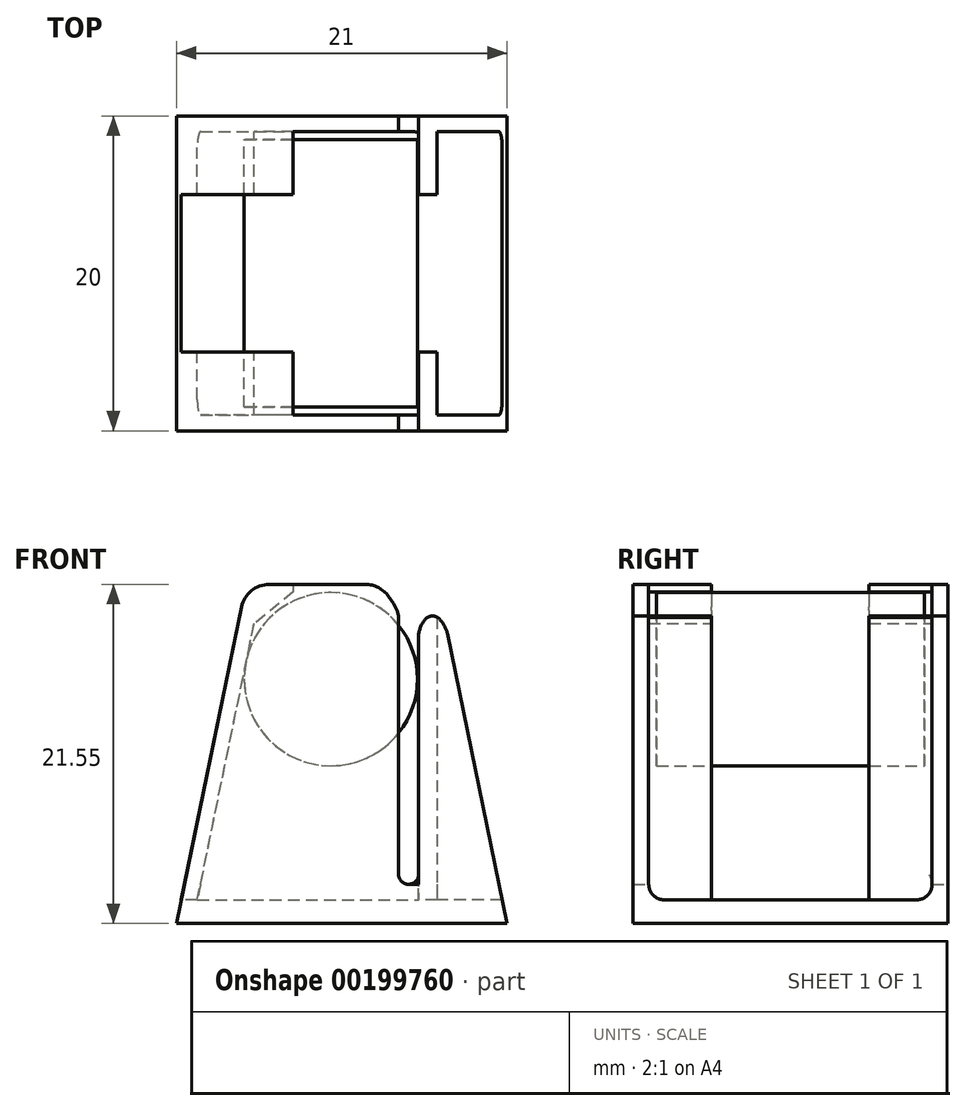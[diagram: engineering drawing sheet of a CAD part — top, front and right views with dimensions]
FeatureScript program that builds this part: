
annotation { "Feature Type Name" : "Feature", "Feature Type Description" : "" }
export const myFeature = defineFeature(function(context is Context, id is Id, definition is map)
    precondition{}
    {
        {
            var Q0;
            Q0=qCreatedBy(makeId("Front.planeOp"),FACE);
            var sketch = newSketch(context, id + "F0", { "sketchPlane" : qUnion([Q0])});
            skLineSegment(sketch, "E0", {"start": v(-14.75, 0) * mm, "end": v(-10.32, 21.55) * mm});
            skLineSegment(sketch, "E1", {"start": v(-1.82, 21.55) * mm, "end": v(0, 18.96) * mm});
            skLineSegment(sketch, "E2", {"start": v(0, 18.96) * mm, "end": v(1.82, 21.55) * mm});
            skLineSegment(sketch, "E3", {"start": v(1.82, 21.55) * mm, "end": v(6.25, 0) * mm});
            skCircle(sketch, "E4", {"center": v(-6.3, 7.31) * mm, "radius": 5.5 * mm});
            skLineSegment(sketch, "E5", {"start": v(-14.75, 0) * mm, "end": v(6.25, 0) * mm});
            skLineSegment(sketch, "E6", {"start": v(5.94, 1.5) * mm, "end": v(-14.44, 1.5) * mm});
            skLineSegment(sketch, "E7.left", {"start": v(-0.63, 19.86) * mm, "end": v(-0.63, 1.5) * mm});
            skLineSegment(sketch, "E8.0", {"start": v(-13.73, 0) * mm, "end": v(-9.3, 21.55) * mm});
            skLineSegment(sketch, "E9.0", {"start": v(1.82, 21.55) * mm, "end": v(1.82, 1.5) * mm});
            skLineSegment(sketch, "E10", {"start": v(-10.32, 21.55) * mm, "end": v(-1.82, 21.55) * mm});
            skLineSegment(sketch, "E11", {"start": v(-0.63, 2.5) * mm, "end": v(0.63, 2.5) * mm});
            skLineSegment(sketch, "E12", {"start": v(0.63, 1.5) * mm, "end": v(0.63, 19.86) * mm});
            skLineSegment(sketch, "E13.bottom", {"start": v(13.14, 28.72) * mm, "end": v(0.63, 28.72) * mm});
            skLineSegment(sketch, "E13.top", {"start": v(13.14, 19.86) * mm, "end": v(0.63, 19.86) * mm});
            skLineSegment(sketch, "E13.left", {"start": v(13.14, 28.72) * mm, "end": v(13.14, 19.86) * mm});
            skLineSegment(sketch, "E13.right", {"start": v(0.63, 28.72) * mm, "end": v(0.63, 19.86) * mm});
            skSolve(sketch);
        }
        {
            var Q0;
            {var subQ5=sQuery(id+"F0.wireOp",EDGE,"E0");var subQ8=sQuery(id+"F0.wireOp",EDGE,"E10");var subQ10=makeQuery(id+"F0.imprint","INTERSECT",VERTEX,{"derivedFrom":[subQ5,subQ8]});Q0=makeQuery(id+"F0.imprint","IMPRINT",FACE,{"disambiguationData":[TD([[makeQuery(id+"F0.imprint","IMPRINT",EDGE,{"disambiguationData":[TD([[subQ10,1.0]])],"derivedFrom":subQ5}),-1.0]])]});}
            var Q1;
            {var subQ0=sQuery(id+"F0.wireOp",EDGE,"E5");var subQ1=sQuery(id+"F0.wireOp",EDGE,"E0");var subQ2=makeQuery(id+"F0.imprint","INTERSECT",VERTEX,{"derivedFrom":[subQ1,subQ0]});Q1=makeQuery(id+"F0.imprint","IMPRINT",FACE,{"disambiguationData":[TD([[makeQuery(id+"F0.imprint","IMPRINT",EDGE,{"disambiguationData":[TD([[subQ2,-1.0]])],"derivedFrom":subQ1}),-1.0]])]});}
            var Q2;
            {var subQ0=sQuery(id+"F0.wireOp",EDGE,"E7.left");var subQ5=sQuery(id+"F0.wireOp",EDGE,"E6");var subQ6=makeQuery(id+"F0.imprint","INTERSECT",VERTEX,{"derivedFrom":[subQ5,subQ0]});Q2=makeQuery(id+"F0.imprint","IMPRINT",FACE,{"disambiguationData":[TD([[makeQuery(id+"F0.imprint","IMPRINT",EDGE,{"disambiguationData":[TD([[subQ6,-1.0]])],"derivedFrom":subQ5}),1.0]])]});}
            var Q3;
            {var subQ5=sQuery(id+"F0.wireOp",EDGE,"E7.top");Q3=makeQuery(id+"F0.imprint","IMPRINT",FACE,{"disambiguationData":[TD([[makeQuery(id+"F0.imprint","IMPRINT",EDGE,{"derivedFrom":subQ5}),1.0]])]});}
            var Q4;
            {var subQ3=sQuery(id+"F0.wireOp",EDGE,"E9.0");var subQ5=sQuery(id+"F0.wireOp",EDGE,"E6");var subQ7=makeQuery(id+"F0.imprint","INTERSECT",VERTEX,{"derivedFrom":[subQ5,subQ3]});Q4=makeQuery(id+"F0.imprint","IMPRINT",FACE,{"disambiguationData":[TD([[makeQuery(id+"F0.imprint","IMPRINT",EDGE,{"disambiguationData":[TD([[subQ7,-1.0]])],"derivedFrom":subQ5}),1.0]])]});}
            var Q5;
            {var subQ3=sQuery(id+"F0.wireOp",EDGE,"E6");var subQ5=sQuery(id+"F0.wireOp",EDGE,"E9.0");var subQ6=makeQuery(id+"F0.imprint","INTERSECT",VERTEX,{"derivedFrom":[subQ3,subQ5]});Q5=makeQuery(id+"F0.imprint","IMPRINT",FACE,{"disambiguationData":[TD([[makeQuery(id+"F0.imprint","IMPRINT",EDGE,{"disambiguationData":[TD([[subQ6,-1.0]])],"derivedFrom":subQ3}),-1.0]])]});}
            var Q6;
            {var subQ1=sQuery(id+"F0.wireOp",EDGE,"E3");var subQ3=sQuery(id+"F0.wireOp",EDGE,"E6");var subQ4=makeQuery(id+"F0.imprint","INTERSECT",VERTEX,{"derivedFrom":[subQ1,subQ3]});Q6=makeQuery(id+"F0.imprint","IMPRINT",FACE,{"disambiguationData":[TD([[makeQuery(id+"F0.imprint","IMPRINT",EDGE,{"disambiguationData":[TD([[subQ4,-1.0]])],"derivedFrom":subQ3}),-1.0]])]});}
            var Q7;
            {var subQ0=sQuery(id+"F0.wireOp",EDGE,"E5");var subQ1=sQuery(id+"F0.wireOp",EDGE,"E3");var subQ2=makeQuery(id+"F0.imprint","INTERSECT",VERTEX,{"derivedFrom":[subQ1,subQ0]});Q7=makeQuery(id+"F0.imprint","IMPRINT",FACE,{"disambiguationData":[TD([[makeQuery(id+"F0.imprint","IMPRINT",EDGE,{"disambiguationData":[TD([[subQ2,1.0]])],"derivedFrom":subQ1}),-1.0]])]});}
            var Q8;
            {var subQ5=sQuery(id+"F0.wireOp",EDGE,"E11");Q8=makeQuery(id+"F0.imprint","IMPRINT",FACE,{"disambiguationData":[TD([[makeQuery(id+"F0.imprint","IMPRINT",EDGE,{"derivedFrom":subQ5}),-1.0]])]});}
            var Q9;
            {var subQ4=sQuery(id+"F0.wireOp",EDGE,"E10");var subQ7=sQuery(id+"F0.wireOp",EDGE,"E1");var subQ8=makeQuery(id+"F0.imprint","INTERSECT",VERTEX,{"derivedFrom":[subQ7,subQ4]});Q9=makeQuery(id+"F0.imprint","IMPRINT",FACE,{"disambiguationData":[TD([[makeQuery(id+"F0.imprint","IMPRINT",EDGE,{"disambiguationData":[TD([[subQ8,-1.0]])],"derivedFrom":subQ7}),-1.0]])]});}
            var Q10;
            Q10=makeQuery(id+"F0.imprint","IMPRINT",FACE,{"disambiguationData":[TD([[makeQuery(id+"F0.imprint","IMPRINT",EDGE,{"derivedFrom":sQuery(id+"F0.wireOp",EDGE,"E4")}),1.0]])]});
            extrude(context, id + "F1", {"entities" : qUnion([Q0, Q1, Q2, Q3, Q4, Q5, Q6, Q7, Q8, Q9, Q10]), "depth" : 1 * mm});
        }
        {
            var Q0;
            {var subQ2=sQuery(id+"F0.wireOp",EDGE,"E6");var subQ4=sQuery(id+"F0.wireOp",EDGE,"E9.0");var subQ5=makeQuery(id+"F0.imprint","INTERSECT",VERTEX,{"derivedFrom":[subQ2,subQ4]});Q0=makeQuery(id+"F0.imprint","IMPRINT",FACE,{"disambiguationData":[TD([[makeQuery(id+"F0.imprint","IMPRINT",EDGE,{"disambiguationData":[TD([[subQ5,-1.0]])],"derivedFrom":subQ2}),-1.0]])]});}
            var Q1;
            {var subQ0=sQuery(id+"F0.wireOp",EDGE,"E10");var subQ1=sQuery(id+"F0.wireOp",EDGE,"E0");var subQ2=makeQuery(id+"F0.imprint","INTERSECT",VERTEX,{"derivedFrom":[subQ1,subQ0]});Q1=makeQuery(id+"F0.imprint","IMPRINT",FACE,{"disambiguationData":[TD([[makeQuery(id+"F0.imprint","IMPRINT",EDGE,{"disambiguationData":[TD([[subQ2,1.0]])],"derivedFrom":subQ1}),-1.0]])]});}
            extrude(context, id + "F2", {"entities" : qUnion([Q0, Q1]), "operationType" : NewBodyOperationType.ADD, "depth" : 5 * mm, "hasSecondDirection" : true, "secondDirectionOppositeDirection" : false, "secondDirectionDepth" : 1 * mm});
        }
        {
            var Q0;
            {var subQ0=sQuery(id+"F0.wireOp",EDGE,"E5");var subQ1=sQuery(id+"F0.wireOp",EDGE,"E3");var subQ2=makeQuery(id+"F0.imprint","INTERSECT",VERTEX,{"derivedFrom":[subQ1,subQ0]});Q0=makeQuery(id+"F0.imprint","IMPRINT",FACE,{"disambiguationData":[TD([[makeQuery(id+"F0.imprint","IMPRINT",EDGE,{"disambiguationData":[TD([[subQ2,1.0]])],"derivedFrom":subQ1}),-1.0]])]});}
            var Q1;
            {var subQ5=sQuery(id+"F0.wireOp",EDGE,"E7.top");Q1=makeQuery(id+"F0.imprint","IMPRINT",FACE,{"disambiguationData":[TD([[makeQuery(id+"F0.imprint","IMPRINT",EDGE,{"derivedFrom":subQ5}),1.0]])]});}
            var Q2;
            {var subQ3=sQuery(id+"F0.wireOp",EDGE,"E9.0");var subQ5=sQuery(id+"F0.wireOp",EDGE,"E6");var subQ6=makeQuery(id+"F0.imprint","INTERSECT",VERTEX,{"derivedFrom":[subQ5,subQ3]});Q2=makeQuery(id+"F0.imprint","IMPRINT",FACE,{"disambiguationData":[TD([[makeQuery(id+"F0.imprint","IMPRINT",EDGE,{"disambiguationData":[TD([[subQ6,-1.0]])],"derivedFrom":subQ5}),1.0]])]});}
            var Q3;
            {var subQ0=sQuery(id+"F0.wireOp",EDGE,"E7.left");var subQ5=sQuery(id+"F0.wireOp",EDGE,"E6");var subQ6=makeQuery(id+"F0.imprint","INTERSECT",VERTEX,{"derivedFrom":[subQ5,subQ0]});Q3=makeQuery(id+"F0.imprint","IMPRINT",FACE,{"disambiguationData":[TD([[makeQuery(id+"F0.imprint","IMPRINT",EDGE,{"disambiguationData":[TD([[subQ6,-1.0]])],"derivedFrom":subQ5}),1.0]])]});}
            var Q4;
            {var subQ0=sQuery(id+"F0.wireOp",EDGE,"E5");var subQ1=sQuery(id+"F0.wireOp",EDGE,"E0");var subQ2=makeQuery(id+"F0.imprint","INTERSECT",VERTEX,{"derivedFrom":[subQ1,subQ0]});Q4=makeQuery(id+"F0.imprint","IMPRINT",FACE,{"disambiguationData":[TD([[makeQuery(id+"F0.imprint","IMPRINT",EDGE,{"disambiguationData":[TD([[subQ2,-1.0]])],"derivedFrom":subQ1}),-1.0]])]});}
            extrude(context, id + "F3", {"entities" : qUnion([Q0, Q1, Q2, Q3, Q4]), "operationType" : NewBodyOperationType.ADD, "depth" : 20 * mm});
        }
        {
            var Q0;
            {var subQ2=sQuery(id+"F0.wireOp",EDGE,"E6");var subQ4=sQuery(id+"F0.wireOp",EDGE,"E9.0");var subQ5=makeQuery(id+"F0.imprint","INTERSECT",VERTEX,{"derivedFrom":[subQ2,subQ4]});Q0=makeQuery(id+"F0.imprint","IMPRINT",FACE,{"disambiguationData":[TD([[makeQuery(id+"F0.imprint","IMPRINT",EDGE,{"disambiguationData":[TD([[subQ5,-1.0]])],"derivedFrom":subQ2}),-1.0]])]});}
            var Q1;
            {var subQ0=sQuery(id+"F0.wireOp",EDGE,"E10");var subQ1=sQuery(id+"F0.wireOp",EDGE,"E0");var subQ2=makeQuery(id+"F0.imprint","INTERSECT",VERTEX,{"derivedFrom":[subQ1,subQ0]});Q1=makeQuery(id+"F0.imprint","IMPRINT",FACE,{"disambiguationData":[TD([[makeQuery(id+"F0.imprint","IMPRINT",EDGE,{"disambiguationData":[TD([[subQ2,1.0]])],"derivedFrom":subQ1}),-1.0]])]});}
            extrude(context, id + "F4", {"entities" : qUnion([Q0, Q1]), "operationType" : NewBodyOperationType.ADD, "depth" : 20 * mm, "hasSecondDirection" : true, "secondDirectionOppositeDirection" : false, "secondDirectionDepth" : 15 * mm});
        }
        {
            var Q0;
            {var subQ1=sQuery(id+"F0.wireOp",EDGE,"E3");var subQ3=sQuery(id+"F0.wireOp",EDGE,"E6");var subQ4=makeQuery(id+"F0.imprint","INTERSECT",VERTEX,{"derivedFrom":[subQ1,subQ3]});Q0=makeQuery(id+"F0.imprint","IMPRINT",FACE,{"disambiguationData":[TD([[makeQuery(id+"F0.imprint","IMPRINT",EDGE,{"disambiguationData":[TD([[subQ4,-1.0]])],"derivedFrom":subQ3}),-1.0]])]});}
            var Q1;
            {var subQ2=sQuery(id+"F0.wireOp",EDGE,"E6");var subQ4=sQuery(id+"F0.wireOp",EDGE,"E9.0");var subQ5=makeQuery(id+"F0.imprint","INTERSECT",VERTEX,{"derivedFrom":[subQ2,subQ4]});Q1=makeQuery(id+"F0.imprint","IMPRINT",FACE,{"disambiguationData":[TD([[makeQuery(id+"F0.imprint","IMPRINT",EDGE,{"disambiguationData":[TD([[subQ5,-1.0]])],"derivedFrom":subQ2}),-1.0]])]});}
            var Q2;
            {var subQ0=sQuery(id+"F0.wireOp",EDGE,"E5");var subQ1=sQuery(id+"F0.wireOp",EDGE,"E3");var subQ2=makeQuery(id+"F0.imprint","INTERSECT",VERTEX,{"derivedFrom":[subQ1,subQ0]});Q2=makeQuery(id+"F0.imprint","IMPRINT",FACE,{"disambiguationData":[TD([[makeQuery(id+"F0.imprint","IMPRINT",EDGE,{"disambiguationData":[TD([[subQ2,1.0]])],"derivedFrom":subQ1}),-1.0]])]});}
            var Q3;
            {var subQ3=sQuery(id+"F0.wireOp",EDGE,"E9.0");var subQ5=sQuery(id+"F0.wireOp",EDGE,"E6");var subQ6=makeQuery(id+"F0.imprint","INTERSECT",VERTEX,{"derivedFrom":[subQ5,subQ3]});Q3=makeQuery(id+"F0.imprint","IMPRINT",FACE,{"disambiguationData":[TD([[makeQuery(id+"F0.imprint","IMPRINT",EDGE,{"disambiguationData":[TD([[subQ6,-1.0]])],"derivedFrom":subQ5}),1.0]])]});}
            var Q4;
            {var subQ5=sQuery(id+"F0.wireOp",EDGE,"E11");Q4=makeQuery(id+"F0.imprint","IMPRINT",FACE,{"disambiguationData":[TD([[makeQuery(id+"F0.imprint","IMPRINT",EDGE,{"derivedFrom":subQ5}),-1.0]])]});}
            var Q5;
            {var subQ5=sQuery(id+"F0.wireOp",EDGE,"E7.top");Q5=makeQuery(id+"F0.imprint","IMPRINT",FACE,{"disambiguationData":[TD([[makeQuery(id+"F0.imprint","IMPRINT",EDGE,{"derivedFrom":subQ5}),1.0]])]});}
            var Q6;
            {var subQ0=sQuery(id+"F0.wireOp",EDGE,"E7.left");var subQ5=sQuery(id+"F0.wireOp",EDGE,"E6");var subQ6=makeQuery(id+"F0.imprint","INTERSECT",VERTEX,{"derivedFrom":[subQ5,subQ0]});Q6=makeQuery(id+"F0.imprint","IMPRINT",FACE,{"disambiguationData":[TD([[makeQuery(id+"F0.imprint","IMPRINT",EDGE,{"disambiguationData":[TD([[subQ6,-1.0]])],"derivedFrom":subQ5}),1.0]])]});}
            var Q7;
            Q7=makeQuery(id+"F0.imprint","IMPRINT",FACE,{"disambiguationData":[TD([[makeQuery(id+"F0.imprint","IMPRINT",EDGE,{"derivedFrom":sQuery(id+"F0.wireOp",EDGE,"diKSwn5I-yN5J-uPFe-3HvR-bQsWpq5G5K9p")}),-1.0]])]});
            var Q8;
            Q8=makeQuery(id+"F0.imprint","IMPRINT",FACE,{"disambiguationData":[TD([[makeQuery(id+"F0.imprint","IMPRINT",EDGE,{"derivedFrom":sQuery(id+"F0.wireOp",EDGE,"E4")}),1.0]])]});
            var Q9;
            Q9=makeQuery(id+"F0.imprint","IMPRINT",FACE,{"disambiguationData":[TD([[makeQuery(id+"F0.imprint","IMPRINT",EDGE,{"derivedFrom":sQuery(id+"F0.wireOp",EDGE,"E4")}),-1.0]])]});
            var Q10;
            {var subQ0=sQuery(id+"F0.wireOp",EDGE,"E10");var subQ1=sQuery(id+"F0.wireOp",EDGE,"E0");var subQ2=makeQuery(id+"F0.imprint","INTERSECT",VERTEX,{"derivedFrom":[subQ1,subQ0]});Q10=makeQuery(id+"F0.imprint","IMPRINT",FACE,{"disambiguationData":[TD([[makeQuery(id+"F0.imprint","IMPRINT",EDGE,{"disambiguationData":[TD([[subQ2,1.0]])],"derivedFrom":subQ1}),-1.0]])]});}
            var Q11;
            {var subQ0=sQuery(id+"F0.wireOp",EDGE,"E5");var subQ1=sQuery(id+"F0.wireOp",EDGE,"E0");var subQ2=makeQuery(id+"F0.imprint","INTERSECT",VERTEX,{"derivedFrom":[subQ1,subQ0]});Q11=makeQuery(id+"F0.imprint","IMPRINT",FACE,{"disambiguationData":[TD([[makeQuery(id+"F0.imprint","IMPRINT",EDGE,{"disambiguationData":[TD([[subQ2,-1.0]])],"derivedFrom":subQ1}),-1.0]])]});}
            extrude(context, id + "F5", {"entities" : qUnion([Q0, Q1, Q2, Q3, Q4, Q5, Q6, Q7, Q8, Q9, Q10, Q11]), "operationType" : NewBodyOperationType.ADD, "depth" : 20 * mm, "hasSecondDirection" : true, "secondDirectionOppositeDirection" : false, "secondDirectionDepth" : 19 * mm});
        }
        {
            var Q0;
            {var subQ0=sQuery(id+"F0.wireOp",EDGE,"E7.left");var subQ1=sQuery(id+"F0.wireOp",EDGE,"E4");var subQ2=makeQuery(id+"F0.imprint","INTERSECT",VERTEX,{"disambiguationData":[OD(0.0)],"derivedFrom":[subQ1,subQ0]});Q0=makeQuery(id+"F0.imprint","IMPRINT",FACE,{"disambiguationData":[TD([[makeQuery(id+"F0.imprint","IMPRINT",EDGE,{"disambiguationData":[TD([[subQ2,-1.0]])],"derivedFrom":subQ1}),1.0]])]});}
            var Q1;
            {var subQ0=sQuery(id+"F0.wireOp",EDGE,"E7.left");var subQ1=sQuery(id+"F0.wireOp",EDGE,"E4");var subQ2=makeQuery(id+"F0.imprint","INTERSECT",VERTEX,{"disambiguationData":[OD(0.0)],"derivedFrom":[subQ1,subQ0]});Q1=makeQuery(id+"F0.imprint","IMPRINT",FACE,{"disambiguationData":[TD([[makeQuery(id+"F0.imprint","IMPRINT",EDGE,{"disambiguationData":[TD([[subQ2,1.0]])],"derivedFrom":subQ1}),1.0]])]});}
            extrude(context, id + "F6", {"entities" : qUnion([Q0, Q1]), "depth" : 18.5 * mm, "hasSecondDirection" : true, "secondDirectionOppositeDirection" : false, "secondDirectionDepth" : 1.5 * mm});
        }
        {
            var Q0;
            Q0=makeQuery(id+"F5.boolean.opBoolean","INTERSECT",EDGE,{"disambiguationData":[OD(0.0)],"derivedFrom":[makeQuery(id+"F3.opExtrude","SWEPT_FACE",FACE,{"disambiguationData":[OSD([sQuery(id+"F0.wireOp",EDGE,"E6")])]}),makeQuery(id+"F5.opExtrude","CAP_FACE",FACE,{"disambiguationData":[OSD([sQuery(id+"F0.wireOp",EDGE,"E0"),sQuery(id+"F0.wireOp",EDGE,"E1"),sQuery(id+"F0.wireOp",EDGE,"E2"),sQuery(id+"F0.wireOp",EDGE,"E3"),sQuery(id+"F0.wireOp",EDGE,"E5"),sQuery(id+"F0.wireOp",EDGE,"E7.top"),sQuery(id+"F0.wireOp",EDGE,"E7.left"),sQuery(id+"F0.wireOp",EDGE,"E7.right"),sQuery(id+"F0.wireOp",EDGE,"E10"),sQuery(id+"F0.wireOp",EDGE,"E11")])],"isStart":true})]});
            var Q1;
            Q1=makeQuery(id+"F4.opExtrude","SWEPT_EDGE",EDGE,{"disambiguationData":[OSD([sQuery(id+"F0.wireOp",EDGE,"E6"),sQuery(id+"F0.wireOp",EDGE,"E9.0")])]});
            var Q2;
            {var subQ0=sQuery(id+"F0.wireOp",EDGE,"E6");Q2=makeQuery(id+"F4.opExtrude","CAP_EDGE",EDGE,{"disambiguationData":[OSD([subQ0]),TDD([makeQuery(id+"F0.imprint","IMPRINT",EDGE,{"disambiguationData":[TD([[makeQuery(id+"F0.imprint","INTERSECT",VERTEX,{"derivedFrom":[subQ0,sQuery(id+"F0.wireOp",EDGE,"E9.0")]}),-1.0]])],"derivedFrom":subQ0})])],"isStart":true});}
            var Q3;
            Q3=makeQuery(id+"F3.boolean.opBoolean","INTERSECT",EDGE,{"disambiguationData":[OD(0.0)],"derivedFrom":[makeQuery(id+"F1.opExtrude","CAP_FACE",FACE,{"disambiguationData":[OSD([sQuery(id+"F0.wireOp",EDGE,"E0"),sQuery(id+"F0.wireOp",EDGE,"E1"),sQuery(id+"F0.wireOp",EDGE,"E2"),sQuery(id+"F0.wireOp",EDGE,"E3"),sQuery(id+"F0.wireOp",EDGE,"E5"),sQuery(id+"F0.wireOp",EDGE,"E7.top"),sQuery(id+"F0.wireOp",EDGE,"E7.left"),sQuery(id+"F0.wireOp",EDGE,"E7.right"),sQuery(id+"F0.wireOp",EDGE,"E10"),sQuery(id+"F0.wireOp",EDGE,"E11"),sQuery(id+"F0.wireOp",EDGE,"diKSwn5I-yN5J-uPFe-3HvR-bQsWpq5G5K9p")])],"isStart":false}),makeQuery(id+"F3.opExtrude","SWEPT_FACE",FACE,{"disambiguationData":[OSD([sQuery(id+"F0.wireOp",EDGE,"E6")])]})]});
            var Q4;
            Q4=makeQuery(id+"F2.opExtrude","SWEPT_EDGE",EDGE,{"disambiguationData":[OSD([sQuery(id+"F0.wireOp",EDGE,"E6"),sQuery(id+"F0.wireOp",EDGE,"E9.0")])]});
            var Q5;
            {var subQ0=sQuery(id+"F0.wireOp",EDGE,"E6");Q5=makeQuery(id+"F2.opExtrude","CAP_EDGE",EDGE,{"disambiguationData":[OSD([subQ0]),TDD([makeQuery(id+"F0.imprint","IMPRINT",EDGE,{"disambiguationData":[TD([[makeQuery(id+"F0.imprint","INTERSECT",VERTEX,{"derivedFrom":[subQ0,sQuery(id+"F0.wireOp",EDGE,"E9.0")]}),-1.0]])],"derivedFrom":subQ0})])],"isStart":false});}
            var Q6;
            Q6=makeQuery(id+"F5.boolean.opBoolean","INTERSECT",EDGE,{"disambiguationData":[OD(1.0)],"derivedFrom":[makeQuery(id+"F3.opExtrude","SWEPT_FACE",FACE,{"disambiguationData":[OSD([sQuery(id+"F0.wireOp",EDGE,"E6")])]}),makeQuery(id+"F5.opExtrude","CAP_FACE",FACE,{"disambiguationData":[OSD([sQuery(id+"F0.wireOp",EDGE,"E0"),sQuery(id+"F0.wireOp",EDGE,"E1"),sQuery(id+"F0.wireOp",EDGE,"E2"),sQuery(id+"F0.wireOp",EDGE,"E3"),sQuery(id+"F0.wireOp",EDGE,"E5"),sQuery(id+"F0.wireOp",EDGE,"E7.top"),sQuery(id+"F0.wireOp",EDGE,"E7.left"),sQuery(id+"F0.wireOp",EDGE,"E7.right"),sQuery(id+"F0.wireOp",EDGE,"E10"),sQuery(id+"F0.wireOp",EDGE,"E11")])],"isStart":true})]});
            var Q7;
            Q7=makeQuery(id+"F4.opExtrude","SWEPT_EDGE",EDGE,{"disambiguationData":[OSD([sQuery(id+"F0.wireOp",EDGE,"E6"),sQuery(id+"F0.wireOp",EDGE,"E8.0")])]});
            var Q8;
            {var subQ0=sQuery(id+"F0.wireOp",EDGE,"E6");Q8=makeQuery(id+"F4.opExtrude","CAP_EDGE",EDGE,{"disambiguationData":[OSD([subQ0]),TDD([makeQuery(id+"F0.imprint","IMPRINT",EDGE,{"disambiguationData":[TD([[makeQuery(id+"F0.imprint","INTERSECT",VERTEX,{"derivedFrom":[sQuery(id+"F0.wireOp",EDGE,"E0"),subQ0]}),1.0]])],"derivedFrom":subQ0})])],"isStart":true});}
            var Q9;
            Q9=makeQuery(id+"F2.opExtrude","SWEPT_EDGE",EDGE,{"disambiguationData":[OSD([sQuery(id+"F0.wireOp",EDGE,"E6"),sQuery(id+"F0.wireOp",EDGE,"E8.0")])]});
            var Q10;
            {var subQ0=sQuery(id+"F0.wireOp",EDGE,"E6");Q10=makeQuery(id+"F2.opExtrude","CAP_EDGE",EDGE,{"disambiguationData":[OSD([subQ0]),TDD([makeQuery(id+"F0.imprint","IMPRINT",EDGE,{"disambiguationData":[TD([[makeQuery(id+"F0.imprint","INTERSECT",VERTEX,{"derivedFrom":[sQuery(id+"F0.wireOp",EDGE,"E0"),subQ0]}),1.0]])],"derivedFrom":subQ0})])],"isStart":false});}
            var Q11;
            Q11=makeQuery(id+"F3.boolean.opBoolean","INTERSECT",EDGE,{"disambiguationData":[OD(1.0)],"derivedFrom":[makeQuery(id+"F1.opExtrude","CAP_FACE",FACE,{"disambiguationData":[OSD([sQuery(id+"F0.wireOp",EDGE,"E0"),sQuery(id+"F0.wireOp",EDGE,"E1"),sQuery(id+"F0.wireOp",EDGE,"E2"),sQuery(id+"F0.wireOp",EDGE,"E3"),sQuery(id+"F0.wireOp",EDGE,"E5"),sQuery(id+"F0.wireOp",EDGE,"E7.top"),sQuery(id+"F0.wireOp",EDGE,"E7.left"),sQuery(id+"F0.wireOp",EDGE,"E7.right"),sQuery(id+"F0.wireOp",EDGE,"E10"),sQuery(id+"F0.wireOp",EDGE,"E11"),sQuery(id+"F0.wireOp",EDGE,"diKSwn5I-yN5J-uPFe-3HvR-bQsWpq5G5K9p")])],"isStart":false}),makeQuery(id+"F3.opExtrude","SWEPT_FACE",FACE,{"disambiguationData":[OSD([sQuery(id+"F0.wireOp",EDGE,"E6")])]})]});
            var Q12;
            Q12=makeQuery(id+"F2.opExtrude","SWEPT_EDGE",EDGE,{"disambiguationData":[OSD([sQuery(id+"F0.wireOp",EDGE,"E6"),sQuery(id+"F0.wireOp",EDGE,"E7.right")])]});
            var Q13;
            Q13=makeQuery(id+"F4.opExtrude","SWEPT_EDGE",EDGE,{"disambiguationData":[OSD([sQuery(id+"F0.wireOp",EDGE,"E6"),sQuery(id+"F0.wireOp",EDGE,"E7.right")])]});
            fillet(context, id + "F7", {"entities" : qUnion([Q0, Q1, Q2, Q3, Q4, Q5, Q6, Q7, Q8, Q9, Q10, Q11, Q12, Q13]), "radius" : 1 * mm, "tangentPropagation" : true, "allowEdgeOverflow" : false});
        }
        {
            var Q0;
            Q0=makeQuery(id+"F6.opExtrude","SWEPT_BODY",BODY,{"disambiguationData":[OSD([sQuery(id+"F0.wireOp",EDGE,"E4")])]});
            transform(context, id + "F8", {"entities" : qUnion([Q0]), "transformType" : TransformType.TRANSLATION_3D, "dx" : 1.36 * mm, "dy" : 0 * mm, "dz" : 8.21 * mm, "makeCopy" : false});
        }
        {
            var Q0;
            {var subQ0=sQuery(id+"F0.wireOp",EDGE,"E13.top");var subQ1=sQuery(id+"F0.wireOp",EDGE,"E12");var subQ2=sQuery(id+"F0.wireOp",EDGE,"E10");var subQ3=sQuery(id+"F0.wireOp",EDGE,"E5");var subQ4=sQuery(id+"F0.wireOp",EDGE,"E3");var subQ5=sQuery(id+"F0.wireOp",EDGE,"E0");var subQ6=sQuery(id+"F0.wireOp",EDGE,"E6");Q0=makeQuery(id+"F5.boolean.opBoolean","MERGE",FACE,{"derivedFrom":[makeQuery(id+"F4.boolean.opBoolean","MERGE",FACE,{"derivedFrom":[makeQuery(id+"F3.opExtrude","CAP_FACE",FACE,{"disambiguationData":[OSD([subQ5,subQ4,subQ3,subQ6])],"isStart":false}),makeQuery(id+"F4.opExtrude","CAP_FACE",FACE,{"disambiguationData":[OSD([subQ5,subQ6,sQuery(id+"F0.wireOp",EDGE,"E8.0"),subQ2])],"isStart":false}),makeQuery(id+"F4.opExtrude","CAP_FACE",FACE,{"disambiguationData":[OSD([subQ6,sQuery(id+"F0.wireOp",EDGE,"E9.0"),subQ1,subQ0])],"isStart":false})]}),makeQuery(id+"F5.opExtrude","CAP_FACE",FACE,{"disambiguationData":[OSD([subQ5,sQuery(id+"F0.wireOp",EDGE,"E1"),subQ4,subQ3,sQuery(id+"F0.wireOp",EDGE,"E7.left"),subQ2,sQuery(id+"F0.wireOp",EDGE,"E11"),subQ1,subQ0])],"isStart":false})]});}
            var sketch = newSketch(context, id + "F9", { "sketchPlane" : qUnion([Q0])});
            skLineSegment(sketch, "E14", {"start": v(-7.32, 21.55) * mm, "end": v(-7.32, 21.05) * mm});
            skLineSegment(sketch, "E15", {"start": v(-7.32, 21.05) * mm, "end": v(-9.96, 18.93) * mm});
            skLineSegment(sketch, "E16", {"start": v(-9.96, 18.93) * mm, "end": v(-9.96, 21.55) * mm});
            skLineSegment(sketch, "E17", {"start": v(-9.96, 21.55) * mm, "end": v(-7.32, 21.55) * mm});
            skSolve(sketch);
        }
        {
            var Q0;
            Q0=makeQuery(id+"F9.imprint","IMPRINT",FACE,{"disambiguationData":[TD([[makeQuery(id+"F9.imprint","IMPRINT",EDGE,{"derivedFrom":sQuery(id+"F9.wireOp",EDGE,"E14")}),-1.0]])]});
            extrude(context, id + "F10", {"entities" : qUnion([Q0]), "operationType" : NewBodyOperationType.ADD, "oppositeDirection" : true, "depth" : 5 * mm});
        }
        {
            var Q0;
            Q0 = qSketchRegion(id + "F9", true);
            var Q1;
            Q1 = qConstructionFilter(qBodyType(qCreatedBy(id + "F9" ,EDGE), BodyType.WIRE), ConstructionObject.NO);
            extrude(context, id + "F11", {"entities" : qUnion([Q0]), "operationType" : NewBodyOperationType.ADD, "surfaceEntities" : qUnion([Q1]), "oppositeDirection" : true, "depth" : 20 * mm, "hasSecondDirection" : true, "secondDirectionOppositeDirection" : true, "secondDirectionDepth" : 15 * mm});
        }
        {
            var Q0;
            {var subQ0=sQuery(id+"F0.wireOp",EDGE,"E10");var subQ1=sQuery(id+"F0.wireOp",EDGE,"E0");Q0=makeQuery(id+"F2.boolean.opBoolean","MERGE",EDGE,{"derivedFrom":[makeQuery(id+"F1.opExtrude","SWEPT_EDGE",EDGE,{"disambiguationData":[OSD([subQ1,subQ0])]}),makeQuery(id+"F2.opExtrude","SWEPT_EDGE",EDGE,{"disambiguationData":[OSD([subQ1,subQ0])]})]});}
            var Q1;
            Q1=makeQuery(id+"F4.opExtrude","SWEPT_EDGE",EDGE,{"disambiguationData":[OSD([sQuery(id+"F0.wireOp",EDGE,"E0"),sQuery(id+"F0.wireOp",EDGE,"E10")])]});
            var Q2;
            Q2=makeQuery(id+"F5.opExtrude","SWEPT_EDGE",EDGE,{"disambiguationData":[OSD([sQuery(id+"F0.wireOp",EDGE,"E3"),sQuery(id+"F0.wireOp",EDGE,"E13.top")])]});
            var Q3;
            Q3=makeQuery(id+"F1.opExtrude","SWEPT_EDGE",EDGE,{"disambiguationData":[OSD([sQuery(id+"F0.wireOp",EDGE,"E3"),sQuery(id+"F0.wireOp",EDGE,"E13.top")])]});
            var Q4;
            Q4=makeQuery(id+"F1.opExtrude","SWEPT_EDGE",EDGE,{"disambiguationData":[OSD([sQuery(id+"F0.wireOp",EDGE,"E1"),sQuery(id+"F0.wireOp",EDGE,"E10")])]});
            var Q5;
            Q5=makeQuery(id+"F1.opExtrude","SWEPT_EDGE",EDGE,{"disambiguationData":[OSD([sQuery(id+"F0.wireOp",EDGE,"E1"),sQuery(id+"F0.wireOp",EDGE,"E7.left")])]});
            var Q6;
            Q6=makeQuery(id+"F5.opExtrude","SWEPT_EDGE",EDGE,{"disambiguationData":[OSD([sQuery(id+"F0.wireOp",EDGE,"E1"),sQuery(id+"F0.wireOp",EDGE,"E10")])]});
            var Q7;
            Q7=makeQuery(id+"F5.opExtrude","SWEPT_EDGE",EDGE,{"disambiguationData":[OSD([sQuery(id+"F0.wireOp",EDGE,"E1"),sQuery(id+"F0.wireOp",EDGE,"E7.left")])]});
            var Q8;
            Q8=makeQuery(id+"F4.opExtrude","SWEPT_EDGE",EDGE,{"disambiguationData":[OSD([sQuery(id+"F0.wireOp",EDGE,"E2"),sQuery(id+"F0.wireOp",EDGE,"E12"),sQuery(id+"F0.wireOp",EDGE,"E13.top"),sQuery(id+"F0.wireOp",EDGE,"E13.right")])]});
            var Q9;
            {var subQ0=sQuery(id+"F0.wireOp",EDGE,"E13.right");var subQ1=sQuery(id+"F0.wireOp",EDGE,"E13.top");var subQ2=sQuery(id+"F0.wireOp",EDGE,"E12");var subQ3=sQuery(id+"F0.wireOp",EDGE,"E2");Q9=makeQuery(id+"F2.boolean.opBoolean","MERGE",EDGE,{"derivedFrom":[makeQuery(id+"F1.opExtrude","SWEPT_EDGE",EDGE,{"disambiguationData":[OSD([subQ3,subQ2,subQ1,subQ0])]}),makeQuery(id+"F2.opExtrude","SWEPT_EDGE",EDGE,{"disambiguationData":[OSD([subQ3,subQ2,subQ1,subQ0])]})]});}
            fillet(context, id + "F12", {"entities" : qUnion([Q0, Q1, Q2, Q3, Q4, Q5, Q6, Q7, Q8, Q9]), "radius" : 1.8 * mm, "tangentPropagation" : true, "allowEdgeOverflow" : false});
        }
        {
            var Q0;
            Q0=makeQuery(id+"F5.opExtrude","SWEPT_EDGE",EDGE,{"disambiguationData":[OSD([sQuery(id+"F0.wireOp",EDGE,"E7.left"),sQuery(id+"F0.wireOp",EDGE,"E11")])]});
            var Q1;
            Q1=makeQuery(id+"F1.opExtrude","SWEPT_EDGE",EDGE,{"disambiguationData":[OSD([sQuery(id+"F0.wireOp",EDGE,"E7.left"),sQuery(id+"F0.wireOp",EDGE,"E11")])]});
            var Q2;
            Q2=makeQuery(id+"F5.opExtrude","SWEPT_EDGE",EDGE,{"disambiguationData":[OSD([sQuery(id+"F0.wireOp",EDGE,"E11"),sQuery(id+"F0.wireOp",EDGE,"E12")])]});
            var Q3;
            Q3=makeQuery(id+"F1.opExtrude","SWEPT_EDGE",EDGE,{"disambiguationData":[OSD([sQuery(id+"F0.wireOp",EDGE,"E11"),sQuery(id+"F0.wireOp",EDGE,"E12")])]});
            var Q4;
            {var subQ0=sQuery(id+"F0.wireOp",EDGE,"E13.top");Q4=makeQuery(id+"F12.opFillet","BLEND_EDGE",EDGE,{"blendedFrom":[makeQuery(id+"F5.opExtrude","SWEPT_EDGE",EDGE,{"disambiguationData":[OSD([sQuery(id+"F0.wireOp",EDGE,"E3"),subQ0])]}),makeQuery(id+"F4.opExtrude","SWEPT_EDGE",EDGE,{"disambiguationData":[OSD([sQuery(id+"F0.wireOp",EDGE,"E2"),sQuery(id+"F0.wireOp",EDGE,"E12"),subQ0,sQuery(id+"F0.wireOp",EDGE,"E13.right")])]})],"blendedInto":[]});}
            var Q5;
            {var subQ0=sQuery(id+"F0.wireOp",EDGE,"E13.right");var subQ1=sQuery(id+"F0.wireOp",EDGE,"E13.top");var subQ2=sQuery(id+"F0.wireOp",EDGE,"E12");var subQ3=sQuery(id+"F0.wireOp",EDGE,"E2");Q5=makeQuery(id+"F12.opFillet","BLEND_EDGE",EDGE,{"blendedFrom":[makeQuery(id+"F1.opExtrude","SWEPT_EDGE",EDGE,{"disambiguationData":[OSD([sQuery(id+"F0.wireOp",EDGE,"E3"),subQ1])]}),makeQuery(id+"F2.boolean.opBoolean","MERGE",EDGE,{"derivedFrom":[makeQuery(id+"F1.opExtrude","SWEPT_EDGE",EDGE,{"disambiguationData":[OSD([subQ3,subQ2,subQ1,subQ0])]}),makeQuery(id+"F2.opExtrude","SWEPT_EDGE",EDGE,{"disambiguationData":[OSD([subQ3,subQ2,subQ1,subQ0])]})]})],"blendedInto":[]});}
            fillet(context, id + "F13", {"entities" : qUnion([Q0, Q1, Q2, Q3, Q4, Q5]), "radius" : 0.6 * mm, "tangentPropagation" : true, "allowEdgeOverflow" : false});
        }
    });
